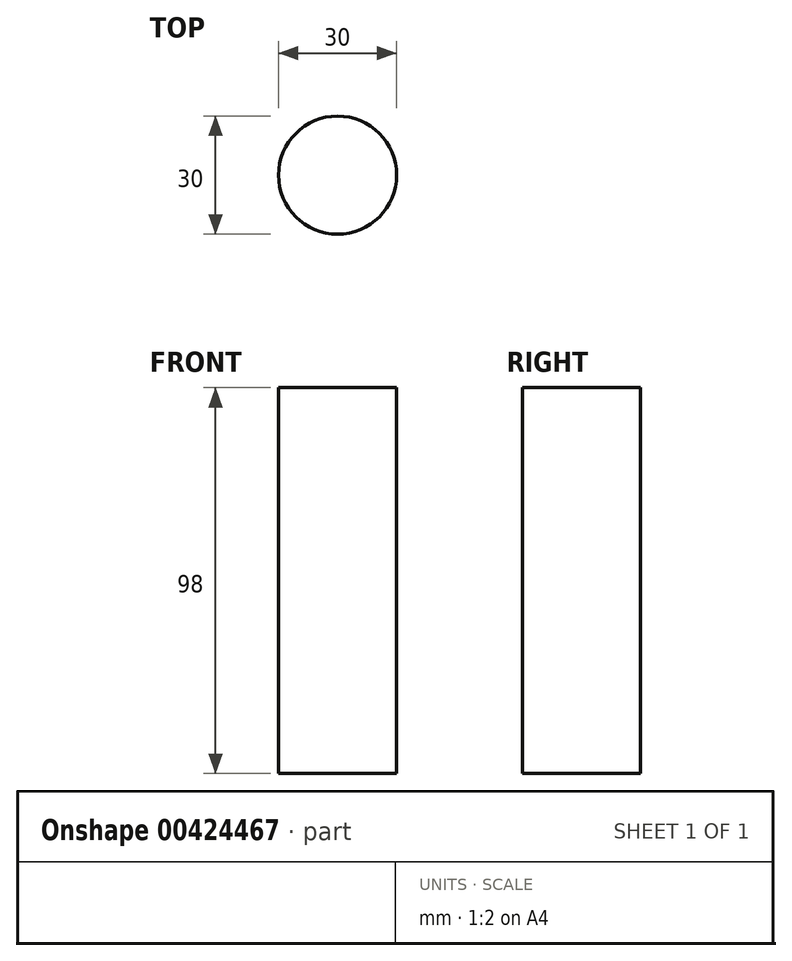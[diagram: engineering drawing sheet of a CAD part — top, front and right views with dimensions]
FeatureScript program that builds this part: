
annotation { "Feature Type Name" : "Feature", "Feature Type Description" : "" }
export const myFeature = defineFeature(function(context is Context, id is Id, definition is map)
    precondition{}
    {
        {
            var Q0;
            Q0=qCreatedBy(makeId("Top.planeOp"),FACE);
            var sketch = newSketch(context, id + "F0", { "sketchPlane" : qUnion([Q0])});
            skLineSegment(sketch, "E0", {"start": v(0, 50) * mm, "end": v(-50, 50) * mm, "construction": true});
            skLineSegment(sketch, "E1", {"start": v(-50, 50) * mm, "end": v(-50, -50) * mm, "construction": true});
            skLineSegment(sketch, "E2", {"start": v(-50, -50) * mm, "end": v(50, -50) * mm, "construction": true});
            skLineSegment(sketch, "E3", {"start": v(50, -50) * mm, "end": v(50, 50) * mm, "construction": true});
            skLineSegment(sketch, "E4", {"start": v(50, 50) * mm, "end": v(0, 50) * mm, "construction": true});
            skLineSegment(sketch, "E5", {"start": v(0, 50) * mm, "end": v(0, 48) * mm, "construction": true});
            skLineSegment(sketch, "E6", {"start": v(0, 48) * mm, "end": v(0, 33) * mm, "construction": true});
            skCircle(sketch, "E7", {"center": v(0, 33) * mm, "radius": 15 * mm});
            skSolve(sketch);
        }
        {
            var Q0;
            Q0=makeQuery(id+"F0.imprint","IMPRINT",FACE,{"disambiguationData":[TD([[makeQuery(id+"F0.imprint","IMPRINT",EDGE,{"derivedFrom":sQuery(id+"F0.wireOp",EDGE,"E7")}),1.0]])]});
            extrude(context, id + "F1", {"entities" : qUnion([Q0]), "depth" : 98 * mm});
        }
    });
